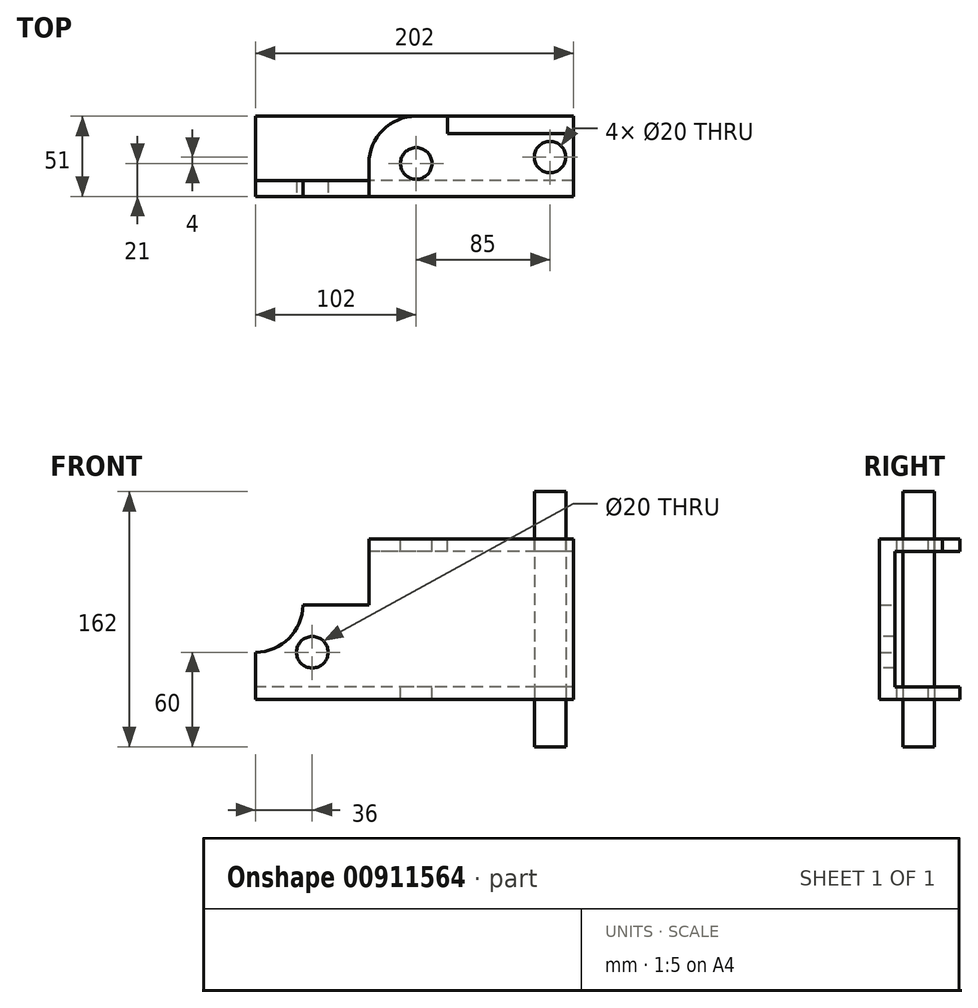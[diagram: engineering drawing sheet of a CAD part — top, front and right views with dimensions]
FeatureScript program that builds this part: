
annotation { "Feature Type Name" : "Feature", "Feature Type Description" : "" }
export const myFeature = defineFeature(function(context is Context, id is Id, definition is map)
    precondition{}
    {
        {
            var Q0;
            Q0=qCreatedBy(makeId("Front.planeOp"),FACE);
            var sketch = newSketch(context, id + "F0", { "sketchPlane" : qUnion([Q0])});
            skLineSegment(sketch, "E0", {"start": v(0, 0) * mm, "end": v(0, 102) * mm});
            skLineSegment(sketch, "E1", {"start": v(0, 102) * mm, "end": v(-130, 102) * mm});
            skLineSegment(sketch, "E2", {"start": v(-130, 102) * mm, "end": v(-130, 60) * mm});
            skLineSegment(sketch, "E3", {"start": v(-130, 60) * mm, "end": v(-172, 60) * mm});
            skLineSegment(sketch, "E4", {"start": v(-172, 60) * mm, "end": v(-172, 30) * mm});
            skLineSegment(sketch, "E5", {"start": v(-172, 30) * mm, "end": v(-202, 30) * mm});
            skLineSegment(sketch, "E6", {"start": v(-202, 30) * mm, "end": v(-202, 0) * mm});
            skLineSegment(sketch, "E7", {"start": v(-202, 0) * mm, "end": v(0, 0) * mm});
            skSolve(sketch);
        }
        {
            var Q0;
            Q0=makeQuery(id+"F0.imprint","IMPRINT",FACE,{"disambiguationData":[TD([[makeQuery(id+"F0.imprint","IMPRINT",EDGE,{"derivedFrom":sQuery(id+"F0.wireOp",EDGE,"E0")}),1.0]])]});
            extrude(context, id + "F1", {"entities" : qUnion([Q0]), "depth" : 10 * mm, "offsetDistance" : 25 * mm});
        }
        {
            var Q0;
            Q0=makeQuery(id+"F1.opExtrude","SWEPT_EDGE",EDGE,{"disambiguationData":[OSD([sQuery(id+"F0.wireOp",EDGE,"E4"),sQuery(id+"F0.wireOp",EDGE,"E5")])]});
            fillet(context, id + "F2", {"entities" : qUnion([Q0]), "radius" : 30 * mm, "tangentPropagation" : true, "allowEdgeOverflow" : false});
        }
        {
            var Q0;
            Q0=makeQuery(id+"F1.opExtrude","CAP_FACE",FACE,{"disambiguationData":[OSD([sQuery(id+"F0.wireOp",EDGE,"E0"),sQuery(id+"F0.wireOp",EDGE,"E1"),sQuery(id+"F0.wireOp",EDGE,"E2"),sQuery(id+"F0.wireOp",EDGE,"E3"),sQuery(id+"F0.wireOp",EDGE,"E4"),sQuery(id+"F0.wireOp",EDGE,"E5"),sQuery(id+"F0.wireOp",EDGE,"E6"),sQuery(id+"F0.wireOp",EDGE,"E7")])],"isStart":false});
            var sketch = newSketch(context, id + "F3", { "sketchPlane" : qUnion([Q0])});
            skLineSegment(sketch, "E8", {"start": v(-202, 30) * mm, "end": v(-166, 30) * mm});
            skSolve(sketch);
        }
        {
            var Q0;
            Q0=sQuery(id+"F3.wireOp",VERTEX,"E8.end");
            var Q1;
            Q1=makeQuery(id+"F1.opExtrude","SWEPT_BODY",BODY,{"disambiguationData":[OSD([sQuery(id+"F0.wireOp",EDGE,"E0"),sQuery(id+"F0.wireOp",EDGE,"E1"),sQuery(id+"F0.wireOp",EDGE,"E2"),sQuery(id+"F0.wireOp",EDGE,"E3"),sQuery(id+"F0.wireOp",EDGE,"E4"),sQuery(id+"F0.wireOp",EDGE,"E5"),sQuery(id+"F0.wireOp",EDGE,"E6"),sQuery(id+"F0.wireOp",EDGE,"E7")])]});
            hole(context, id + "F4", {"style" : HoleStyle.SIMPLE, "endStyle" : HoleEndStyle.THROUGH, "holeDiameter" : 20 * mm, "majorDiameter" : 5 * mm, "isTappedThrough" : true, "tappedDepth" : 12 * mm, "tapClearance" : 3, "locations" : qUnion([Q0]), "scope" : qUnion([Q1])});
        }
        {
            var Q0;
            Q0=qCreatedBy(makeId("Top.planeOp"),FACE);
            var sketch = newSketch(context, id + "F5", { "sketchPlane" : qUnion([Q0])});
            skLineSegment(sketch, "E9", {"start": v(0, 0) * mm, "end": v(-202, 0) * mm});
            skLineSegment(sketch, "E10", {"start": v(-202, 0) * mm, "end": v(-202, 41) * mm});
            skLineSegment(sketch, "E11", {"start": v(-202, 41) * mm, "end": v(0, 41) * mm});
            skLineSegment(sketch, "E12", {"start": v(0, 41) * mm, "end": v(0, 0) * mm});
            skSolve(sketch);
        }
        {
            var Q0;
            Q0=makeQuery(id+"F5.imprint","IMPRINT",FACE,{"disambiguationData":[TD([[makeQuery(id+"F5.imprint","IMPRINT",EDGE,{"derivedFrom":sQuery(id+"F5.wireOp",EDGE,"E9")}),-1.0]])]});
            extrude(context, id + "F6", {"entities" : qUnion([Q0]), "operationType" : NewBodyOperationType.ADD, "depth" : 8 * mm, "offsetDistance" : 25 * mm});
        }
        {
            var Q0;
            Q0=qCreatedBy(makeId("Top.planeOp"),FACE);
            var sketch = newSketch(context, id + "F7", { "sketchPlane" : qUnion([Q0])});
            skLineSegment(sketch, "E13", {"start": v(0, 0) * mm, "end": v(0, 15) * mm});
            skLineSegment(sketch, "E14", {"start": v(0, 15) * mm, "end": v(-15, 15) * mm});
            skCircle(sketch, "E15", {"center": v(-15, 15) * mm, "radius": 10 * mm});
            skSolve(sketch);
        }
        {
            var Q0;
            Q0=sQuery(id+"F7.wireOp",VERTEX,"E14.end");
            var Q1;
            Q1=makeQuery(id+"F1.opExtrude","SWEPT_BODY",BODY,{"disambiguationData":[OSD([sQuery(id+"F0.wireOp",EDGE,"E0"),sQuery(id+"F0.wireOp",EDGE,"E1"),sQuery(id+"F0.wireOp",EDGE,"E2"),sQuery(id+"F0.wireOp",EDGE,"E3"),sQuery(id+"F0.wireOp",EDGE,"E4"),sQuery(id+"F0.wireOp",EDGE,"E5"),sQuery(id+"F0.wireOp",EDGE,"E6"),sQuery(id+"F0.wireOp",EDGE,"E7")])]});
            hole(context, id + "F8", {"style" : HoleStyle.SIMPLE, "endStyle" : HoleEndStyle.THROUGH, "oppositeDirection" : true, "holeDiameter" : 20 * mm, "majorDiameter" : 5 * mm, "isTappedThrough" : true, "tappedDepth" : 12 * mm, "tapClearance" : 3, "locations" : qUnion([Q0]), "scope" : qUnion([Q1])});
        }
        {
            var Q0;
            Q0=makeQuery(id+"F1.opExtrude","SWEPT_FACE",FACE,{"disambiguationData":[OSD([sQuery(id+"F0.wireOp",EDGE,"E1")])]});
            var sketch = newSketch(context, id + "F9", { "sketchPlane" : qUnion([Q0])});
            skLineSegment(sketch, "E16", {"start": v(0, 0) * mm, "end": v(0, 30) * mm});
            skLineSegment(sketch, "E17", {"start": v(0, 30) * mm, "end": v(-80, 30) * mm});
            skLineSegment(sketch, "E18", {"start": v(-80, 30) * mm, "end": v(-80, 41) * mm});
            skLineSegment(sketch, "E19", {"start": v(-80, 41) * mm, "end": v(-130, 41) * mm});
            skLineSegment(sketch, "E20", {"start": v(-130, 41) * mm, "end": v(-130, 0) * mm});
            skLineSegment(sketch, "E21", {"start": v(-130, 0) * mm, "end": v(0, 0) * mm});
            skSolve(sketch);
        }
        {
            var Q0;
            Q0=makeQuery(id+"F9.imprint","IMPRINT",FACE,{"disambiguationData":[TD([[makeQuery(id+"F9.imprint","IMPRINT",EDGE,{"derivedFrom":sQuery(id+"F9.wireOp",EDGE,"E16")}),1.0]])]});
            extrude(context, id + "F10", {"entities" : qUnion([Q0]), "operationType" : NewBodyOperationType.ADD, "oppositeDirection" : true, "depth" : 8 * mm, "offsetDistance" : 25 * mm});
        }
        {
            var Q0;
            Q0=makeQuery(id+"F10.opExtrude","SWEPT_EDGE",EDGE,{"disambiguationData":[OSD([sQuery(id+"F9.wireOp",EDGE,"E19"),sQuery(id+"F9.wireOp",EDGE,"E20")])]});
            fillet(context, id + "F11", {"entities" : qUnion([Q0]), "radius" : 30 * mm, "tangentPropagation" : true, "allowEdgeOverflow" : false});
        }
        {
            var Q0;
            Q0=makeQuery(id+"F10.boolean.opBoolean","MERGE",FACE,{"derivedFrom":[makeQuery(id+"F1.opExtrude","SWEPT_FACE",FACE,{"disambiguationData":[OSD([sQuery(id+"F0.wireOp",EDGE,"E1")])]}),makeQuery(id+"F10.opExtrude","CAP_FACE",FACE,{"disambiguationData":[OSD([sQuery(id+"F9.wireOp",EDGE,"E16"),sQuery(id+"F9.wireOp",EDGE,"E17"),sQuery(id+"F9.wireOp",EDGE,"E18"),sQuery(id+"F9.wireOp",EDGE,"E19"),sQuery(id+"F9.wireOp",EDGE,"E20"),sQuery(id+"F9.wireOp",EDGE,"E21")])],"isStart":true})]});
            var sketch = newSketch(context, id + "F12", { "sketchPlane" : qUnion([Q0])});
            skLineSegment(sketch, "E22", {"start": v(-130, -10) * mm, "end": v(-130, 11) * mm});
            skLineSegment(sketch, "E23", {"start": v(-130, 11) * mm, "end": v(-100, 11) * mm});
            skLineSegment(sketch, "E24", {"start": v(0, -10) * mm, "end": v(0, 15) * mm});
            skPoint(sketch, "E25.endSnap0", {"position": v(-40, 30) * mm});
            skLineSegment(sketch, "E26", {"start": v(0, 15) * mm, "end": v(-15, 15) * mm});
            skCircle(sketch, "E27", {"center": v(-100, 11) * mm, "radius": 20 * mm});
            skCircle(sketch, "E28", {"center": v(-15, 15) * mm, "radius": 18.88 * mm});
            skSolve(sketch);
        }
        {
            var Q0;
            Q0=sQuery(id+"F12.wireOp",VERTEX,"E23.end");
            var Q1;
            Q1=makeQuery(id+"F1.opExtrude","SWEPT_BODY",BODY,{"disambiguationData":[OSD([sQuery(id+"F0.wireOp",EDGE,"E0"),sQuery(id+"F0.wireOp",EDGE,"E1"),sQuery(id+"F0.wireOp",EDGE,"E2"),sQuery(id+"F0.wireOp",EDGE,"E3"),sQuery(id+"F0.wireOp",EDGE,"E4"),sQuery(id+"F0.wireOp",EDGE,"E5"),sQuery(id+"F0.wireOp",EDGE,"E6"),sQuery(id+"F0.wireOp",EDGE,"E7")])]});
            hole(context, id + "F13", {"style" : HoleStyle.SIMPLE, "endStyle" : HoleEndStyle.THROUGH, "holeDiameter" : 20 * mm, "majorDiameter" : 5 * mm, "isTappedThrough" : true, "tappedDepth" : 12 * mm, "tapClearance" : 3, "locations" : qUnion([Q0]), "scope" : qUnion([Q1])});
        }
        {
            var Q0;
            Q0=sQuery(id+"F12.wireOp",VERTEX,"E26.end");
            var Q1;
            Q1=makeQuery(id+"F1.opExtrude","SWEPT_BODY",BODY,{"disambiguationData":[OSD([sQuery(id+"F0.wireOp",EDGE,"E0"),sQuery(id+"F0.wireOp",EDGE,"E1"),sQuery(id+"F0.wireOp",EDGE,"E2"),sQuery(id+"F0.wireOp",EDGE,"E3"),sQuery(id+"F0.wireOp",EDGE,"E4"),sQuery(id+"F0.wireOp",EDGE,"E5"),sQuery(id+"F0.wireOp",EDGE,"E6"),sQuery(id+"F0.wireOp",EDGE,"E7")])]});
            hole(context, id + "F14", {"style" : HoleStyle.SIMPLE, "endStyle" : HoleEndStyle.THROUGH, "holeDiameter" : 20 * mm, "majorDiameter" : 5 * mm, "isTappedThrough" : true, "tappedDepth" : 12 * mm, "tapClearance" : 3, "locations" : qUnion([Q0]), "scope" : qUnion([Q1])});
        }
        {
            var Q0;
            Q0=makeQuery(id+"F10.boolean.opBoolean","MERGE",FACE,{"derivedFrom":[makeQuery(id+"F1.opExtrude","SWEPT_FACE",FACE,{"disambiguationData":[OSD([sQuery(id+"F0.wireOp",EDGE,"E1")])]}),makeQuery(id+"F10.opExtrude","CAP_FACE",FACE,{"disambiguationData":[OSD([sQuery(id+"F9.wireOp",EDGE,"E16"),sQuery(id+"F9.wireOp",EDGE,"E17"),sQuery(id+"F9.wireOp",EDGE,"E18"),sQuery(id+"F9.wireOp",EDGE,"E19"),sQuery(id+"F9.wireOp",EDGE,"E20"),sQuery(id+"F9.wireOp",EDGE,"E21")])],"isStart":true})]});
            var sketch = newSketch(context, id + "F15", { "sketchPlane" : qUnion([Q0])});
            skCircle(sketch, "E29", {"center": v(-15, 15) * mm, "radius": 9.99 * mm});
            skSolve(sketch);
        }
        {
            var Q0;
            Q0=makeQuery(id+"F15.imprint","IMPRINT",FACE,{"disambiguationData":[TD([[makeQuery(id+"F15.imprint","IMPRINT",EDGE,{"derivedFrom":sQuery(id+"F15.wireOp",EDGE,"E29")}),1.0]])]});
            extrude(context, id + "F16", {"entities" : qUnion([Q0]), "depth" : 30 * mm, "offsetDistance" : 25 * mm});
        }
        {
            var Q0;
            Q0=makeQuery(id+"F16.opExtrude","CAP_FACE",FACE,{"disambiguationData":[OSD([sQuery(id+"F15.wireOp",EDGE,"E29")])],"isStart":true});
            var sketch = newSketch(context, id + "F17", { "sketchPlane" : qUnion([Q0])});
            skCircle(sketch, "E30", {"center": v(-15, -15) * mm, "radius": 10 * mm});
            skSolve(sketch);
        }
        {
            var Q0;
            Q0=makeQuery(id+"F17.imprint","IMPRINT",FACE,{"disambiguationData":[TD([[makeQuery(id+"F17.imprint","IMPRINT",EDGE,{"derivedFrom":makeQuery(id+"F16.opExtrude","CAP_EDGE",EDGE,{"disambiguationData":[OSD([sQuery(id+"F15.wireOp",EDGE,"E29")])],"isStart":true})}),-1.0]])]});
            extrude(context, id + "F18", {"entities" : qUnion([Q0]), "operationType" : NewBodyOperationType.ADD, "depth" : 132 * mm, "offsetDistance" : 25 * mm});
        }
    });
